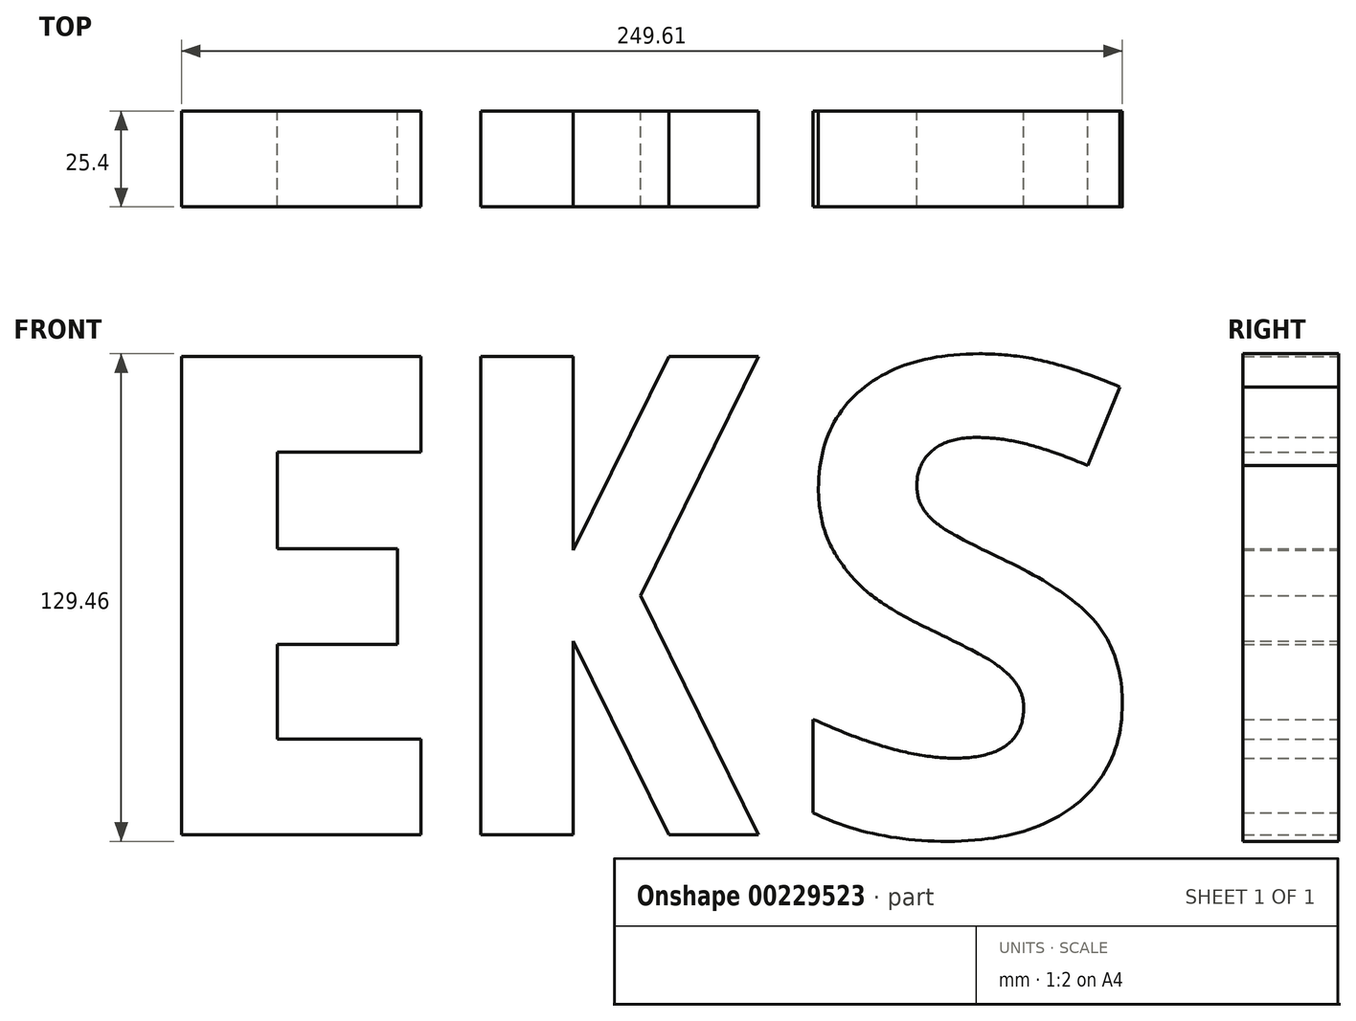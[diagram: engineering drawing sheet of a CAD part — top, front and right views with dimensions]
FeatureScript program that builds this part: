
annotation { "Feature Type Name" : "Feature", "Feature Type Description" : "" }
export const myFeature = defineFeature(function(context is Context, id is Id, definition is map)
    precondition{}
    {
        {
            var Q0;
            Q0=qCreatedBy(makeId("Front.planeOp"),FACE);
            var sketch = newSketch(context, id + "F0", { "sketchPlane" : qUnion([Q0])});
            skLineSegment(sketch, "E0.bottom", {"start": v(12.3, -63.5) * mm, "end": v(-12.3, -63.5) * mm});
            skLineSegment(sketch, "E0.top", {"start": v(12.3, 63.5) * mm, "end": v(-12.3, 63.5) * mm});
            skLineSegment(sketch, "E0.left", {"start": v(12.3, -63.5) * mm, "end": v(12.3, -12.05) * mm});
            skLineSegment(sketch, "E0.right", {"start": v(-12.3, -63.5) * mm, "end": v(-12.3, 63.5) * mm});
            skPoint(sketch, "E0.middle", {"position": v(0, 0) * mm});
            skLineSegment(sketch, "E1", {"start": v(37.6, 63.5) * mm, "end": v(61.45, 63.5) * mm});
            skLineSegment(sketch, "E2", {"start": v(61.45, 63.5) * mm, "end": v(30.22, 0) * mm});
            skLineSegment(sketch, "E3", {"start": v(30.22, 0) * mm, "end": v(61.45, -63.5) * mm});
            skLineSegment(sketch, "E4", {"start": v(61.45, -63.5) * mm, "end": v(37.6, -63.5) * mm});
            skLineSegment(sketch, "E5", {"start": v(37.6, -63.5) * mm, "end": v(12.3, -12.05) * mm});
            skLineSegment(sketch, "E6", {"start": v(37.6, 63.5) * mm, "end": v(12.3, 12.05) * mm});
            skLineSegment(sketch, "E7.trimOffspring", {"start": v(12.3, 12.05) * mm, "end": v(12.3, 63.5) * mm});
            skText(sketch, "E8", { "text": "S", "fontName": "OpenSans-Bold.ttf"});
            skPoint(sketch, "E9", {"position": v(77.31, 27.25) * mm});
            skLineSegment(sketch, "E10", {"start": v(77.31, 27.25) * mm, "end": v(77.31, 63.5) * mm});
            skLineSegment(sketch, "E11", {"start": v(-28.15, 63.5) * mm, "end": v(-28.15, 38.1) * mm});
            skLineSegment(sketch, "E12", {"start": v(-28.15, 38.1) * mm, "end": v(-66.25, 38.1) * mm});
            skLineSegment(sketch, "E13", {"start": v(-28.15, -63.5) * mm, "end": v(-28.15, -38.1) * mm});
            skLineSegment(sketch, "E14", {"start": v(-34.32, -13) * mm, "end": v(-34.32, 12.4) * mm});
            skLineSegment(sketch, "E15", {"start": v(-66.25, 38.1) * mm, "end": v(-66.25, 12.4) * mm});
            skLineSegment(sketch, "E16", {"start": v(-66.25, 12.4) * mm, "end": v(-34.32, 12.4) * mm});
            skLineSegment(sketch, "E17", {"start": v(-34.32, -13) * mm, "end": v(-66.25, -13) * mm});
            skLineSegment(sketch, "E18", {"start": v(-66.25, -13) * mm, "end": v(-66.25, -38.1) * mm});
            skLineSegment(sketch, "E19", {"start": v(-66.25, -38.1) * mm, "end": v(-28.15, -38.1) * mm});
            skLineSegment(sketch, "E20", {"start": v(-28.15, -63.5) * mm, "end": v(-66.25, -63.5) * mm});
            skLineSegment(sketch, "E21", {"start": v(-28.15, 63.5) * mm, "end": v(-91.65, 63.5) * mm});
            skLineSegment(sketch, "E22", {"start": v(-91.65, 63.5) * mm, "end": v(-91.65, -63.5) * mm});
            skLineSegment(sketch, "E23", {"start": v(-91.65, -63.5) * mm, "end": v(-66.25, -63.5) * mm});
            const initialGuessF0  = {"E8": [0.06778, -0.0635, 1, 0, 0.127]};
            skSetInitialGuess(sketch, initialGuessF0);
            skSolve(sketch);
        }
        {
            var Q0;
            Q0 = qSketchRegion(id + "F0", true);
            extrude(context, id + "F1", {"entities" : qUnion([Q0]), "endBound" : BoundingType.SYMMETRIC, "depth" : 25.4 * mm});
        }
    });
